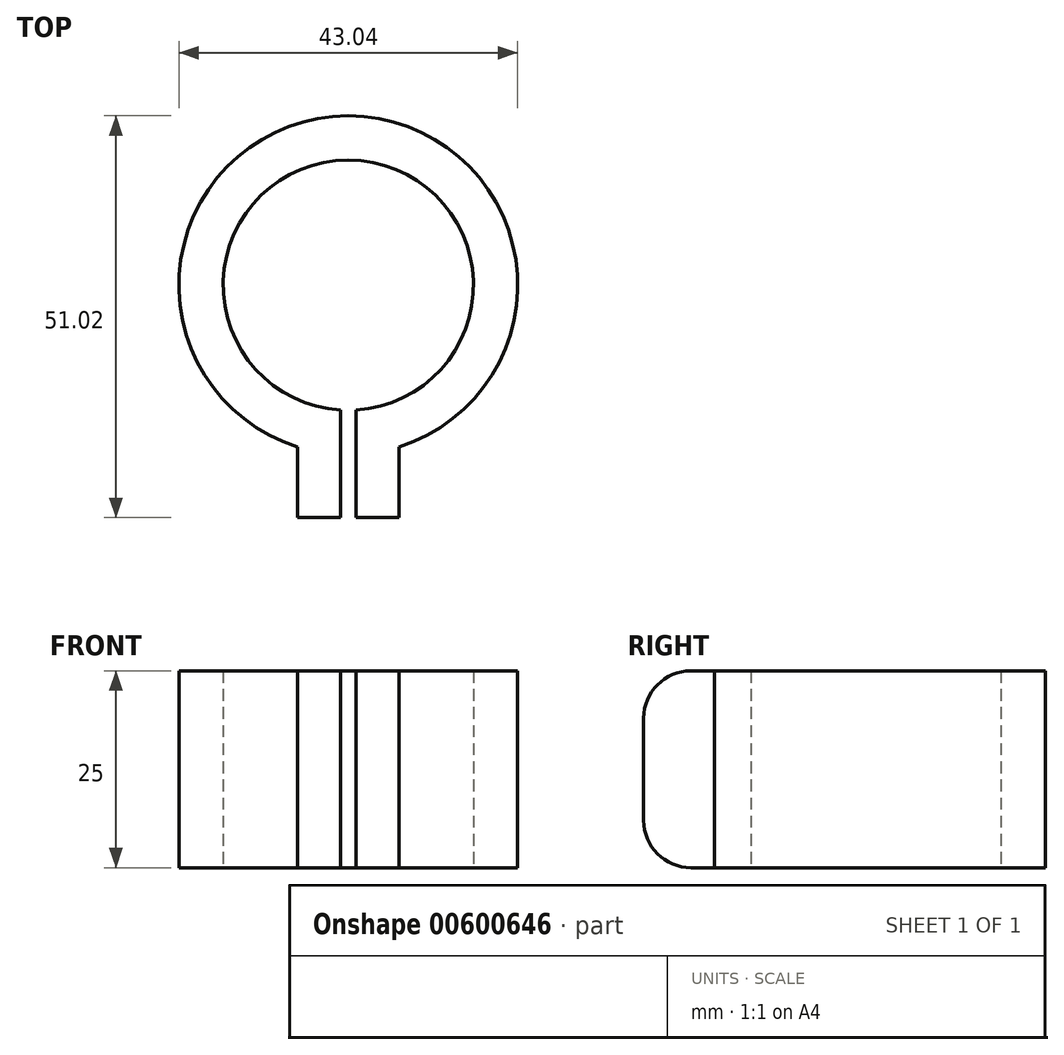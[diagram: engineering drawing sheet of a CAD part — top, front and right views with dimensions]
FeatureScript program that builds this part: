
annotation { "Feature Type Name" : "Feature", "Feature Type Description" : "" }
export const myFeature = defineFeature(function(context is Context, id is Id, definition is map)
    precondition{}
    {
        {
            var Q0;
            Q0=qCreatedBy(makeId("Top.planeOp"),FACE);
            var sketch = newSketch(context, id + "F0", { "sketchPlane" : qUnion([Q0])});
            skCircle(sketch, "E0", {"center": v(0, 0) * mm, "radius": 15.9 * mm});
            skCircle(sketch, "E1", {"center": v(0, 0) * mm, "radius": 21.52 * mm});
            skLineSegment(sketch, "E2", {"start": v(-1, 0) * mm, "end": v(-1, -29.5) * mm});
            skLineSegment(sketch, "E3", {"start": v(-1, -29.5) * mm, "end": v(-6.44, -29.5) * mm});
            skLineSegment(sketch, "E4", {"start": v(-6.44, -29.5) * mm, "end": v(-6.44, -20.54) * mm});
            skLineSegment(sketch, "E5", {"start": v(0, 0) * mm, "end": v(0, 34.65) * mm, "construction": true});
            skLineSegment(sketch, "E6.MirrorCS", {"start": v(1, 0) * mm, "end": v(1, -29.5) * mm});
            skLineSegment(sketch, "E7.MirrorCS", {"start": v(1, -29.5) * mm, "end": v(6.44, -29.5) * mm});
            skLineSegment(sketch, "E8.MirrorCS", {"start": v(6.44, -29.5) * mm, "end": v(6.44, -20.54) * mm});
            skSolve(sketch);
        }
        {
            var Q0;
            {var subQ5=sQuery(id+"F0.wireOp",EDGE,"E2");var subQ7=sQuery(id+"F0.wireOp",EDGE,"E0");var subQ8=makeQuery(id+"F0.imprint","INTERSECT",VERTEX,{"derivedFrom":[subQ7,subQ5]});Q0=makeQuery(id+"F0.imprint","IMPRINT",FACE,{"disambiguationData":[TD([[makeQuery(id+"F0.imprint","IMPRINT",EDGE,{"disambiguationData":[TD([[subQ8,1.0]])],"derivedFrom":subQ7}),-1.0]])]});}
            var Q1;
            {var subQ4=sQuery(id+"F0.wireOp",EDGE,"E3");Q1=makeQuery(id+"F0.imprint","IMPRINT",FACE,{"disambiguationData":[TD([[makeQuery(id+"F0.imprint","IMPRINT",EDGE,{"derivedFrom":subQ4}),-1.0]])]});}
            var Q2;
            {var subQ4=sQuery(id+"F0.wireOp",EDGE,"E7.MirrorCS");Q2=makeQuery(id+"F0.imprint","IMPRINT",FACE,{"disambiguationData":[TD([[makeQuery(id+"F0.imprint","IMPRINT",EDGE,{"derivedFrom":subQ4}),1.0]])]});}
            extrude(context, id + "F1", {"entities" : qUnion([Q0, Q1, Q2]), "depth" : 25 * mm, "offsetDistance" : 25 * mm});
        }
        {
            var Q0;
            Q0=makeQuery(id+"F1.opExtrude","CAP_EDGE",EDGE,{"disambiguationData":[OSD([sQuery(id+"F0.wireOp",EDGE,"E7.MirrorCS")])],"isStart":false});
            var Q1;
            Q1=makeQuery(id+"F1.opExtrude","CAP_EDGE",EDGE,{"disambiguationData":[OSD([sQuery(id+"F0.wireOp",EDGE,"E3")])],"isStart":false});
            var Q2;
            Q2=makeQuery(id+"F1.opExtrude","CAP_EDGE",EDGE,{"disambiguationData":[OSD([sQuery(id+"F0.wireOp",EDGE,"E7.MirrorCS")])],"isStart":true});
            var Q3;
            Q3=makeQuery(id+"F1.opExtrude","CAP_EDGE",EDGE,{"disambiguationData":[OSD([sQuery(id+"F0.wireOp",EDGE,"E3")])],"isStart":true});
            fillet(context, id + "F2", {"entities" : qUnion([Q0, Q1, Q2, Q3]), "tangentPropagation" : true, "radius" : 6 * mm, "defaultsChanged" : true, "vertexSettings" : [], "allowEdgeOverflow" : false});
        }
    });
